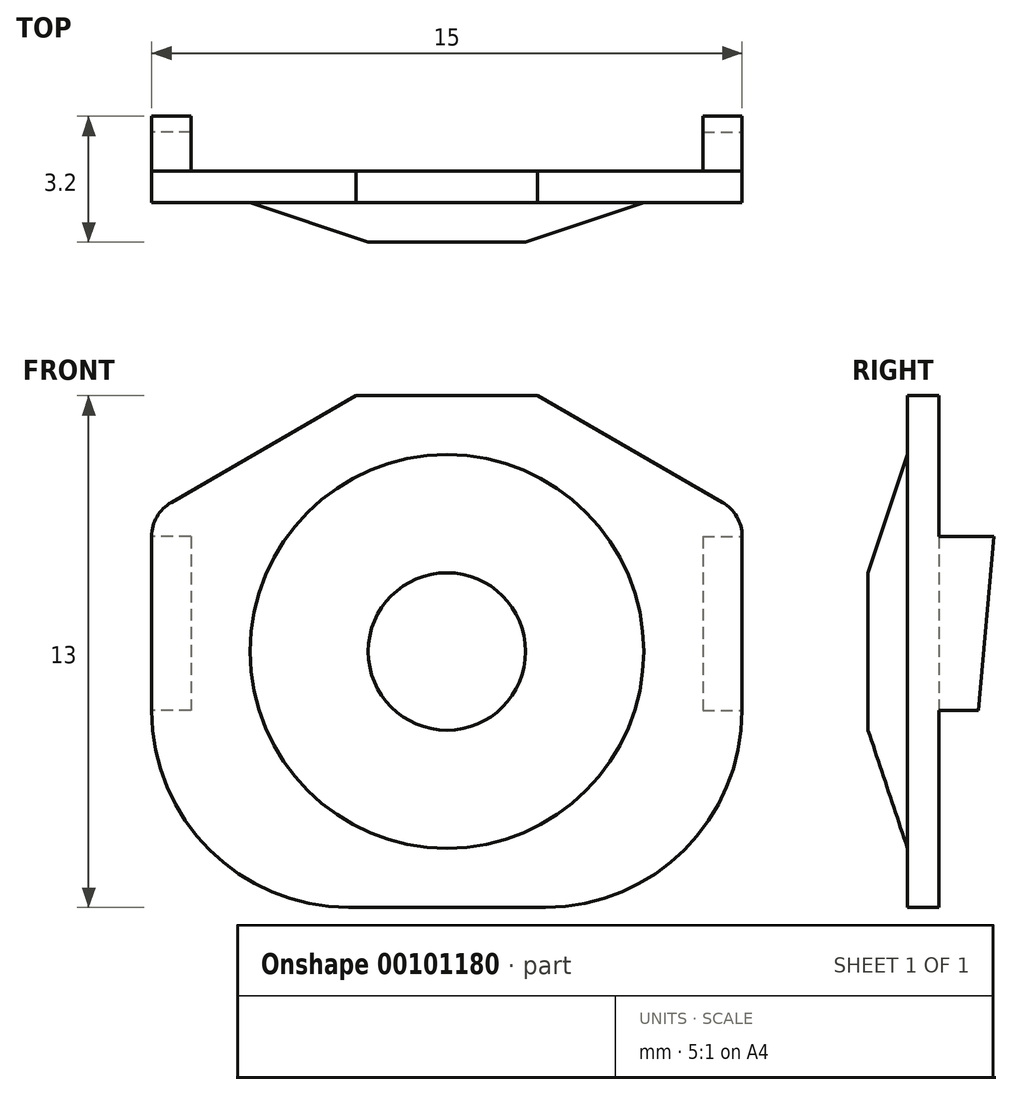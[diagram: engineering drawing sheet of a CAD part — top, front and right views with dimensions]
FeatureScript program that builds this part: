
annotation { "Feature Type Name" : "Feature", "Feature Type Description" : "" }
export const myFeature = defineFeature(function(context is Context, id is Id, definition is map)
    precondition{}
    {
        {
            var Q0;
            Q0=qCreatedBy(makeId("Front.planeOp"),FACE);
            var sketch = newSketch(context, id + "F0", { "sketchPlane" : qUnion([Q0])});
            skLineSegment(sketch, "E0.bottom", {"start": v(2.3, 6.5) * mm, "end": v(-2.3, 6.5) * mm});
            skLineSegment(sketch, "E0.top", {"start": v(7.5, -6.5) * mm, "end": v(-7.5, -6.5) * mm});
            skLineSegment(sketch, "E0.left", {"start": v(7.5, 3.5) * mm, "end": v(7.5, -6.5) * mm});
            skLineSegment(sketch, "E0.right", {"start": v(-7.5, 3.5) * mm, "end": v(-7.5, -6.5) * mm});
            skPoint(sketch, "E0.middle", {"position": v(0, 0) * mm});
            skLineSegment(sketch, "E1", {"start": v(-7.5, 3.5) * mm, "end": v(-2.3, 6.5) * mm});
            skLineSegment(sketch, "E2", {"start": v(2.3, 6.5) * mm, "end": v(7.5, 3.5) * mm});
            skPoint(sketch, "E3.orphan", {"position": v(-7.5, 6.5) * mm});
            skPoint(sketch, "E4.orphan", {"position": v(7.5, 6.5) * mm});
            skSolve(sketch);
        }
        {
            var Q0;
            Q0=makeQuery(id+"F0.imprint","IMPRINT",FACE,{"disambiguationData":[TD([[makeQuery(id+"F0.imprint","IMPRINT",EDGE,{"derivedFrom":sQuery(id+"F0.wireOp",EDGE,"E0.bottom")}),1.0]])]});
            extrude(context, id + "F1", {"entities" : qUnion([Q0]), "offsetDistance" : 25 * mm, "depth" : 0.8 * mm});
        }
        {
            var Q0;
            Q0=makeQuery(id+"F1.opExtrude","SWEPT_EDGE",EDGE,{"disambiguationData":[OSD([sQuery(id+"F0.wireOp",EDGE,"E0.top"),sQuery(id+"F0.wireOp",EDGE,"E0.left")])]});
            var Q1;
            Q1=makeQuery(id+"F1.opExtrude","SWEPT_EDGE",EDGE,{"disambiguationData":[OSD([sQuery(id+"F0.wireOp",EDGE,"E0.top"),sQuery(id+"F0.wireOp",EDGE,"E0.right")])]});
            fillet(context, id + "F2", {"entities" : qUnion([Q0, Q1]), "radius" : 5 * mm, "tangentPropagation" : true, "allowEdgeOverflow" : false});
        }
        {
            var Q0;
            Q0=makeQuery(id+"F1.opExtrude","SWEPT_EDGE",EDGE,{"disambiguationData":[OSD([sQuery(id+"F0.wireOp",EDGE,"E0.left"),sQuery(id+"F0.wireOp",EDGE,"E2")])]});
            var Q1;
            Q1=makeQuery(id+"F1.opExtrude","SWEPT_EDGE",EDGE,{"disambiguationData":[OSD([sQuery(id+"F0.wireOp",EDGE,"E0.right"),sQuery(id+"F0.wireOp",EDGE,"E1")])]});
            fillet(context, id + "F3", {"entities" : qUnion([Q0, Q1]), "radius" : 1 * mm, "tangentPropagation" : true, "allowEdgeOverflow" : false});
        }
        {
            var Q0;
            Q0=makeQuery(id+"F1.opExtrude","CAP_FACE",FACE,{"disambiguationData":[OSD([sQuery(id+"F0.wireOp",EDGE,"E0.bottom"),sQuery(id+"F0.wireOp",EDGE,"E0.top"),sQuery(id+"F0.wireOp",EDGE,"E0.left"),sQuery(id+"F0.wireOp",EDGE,"E0.right"),sQuery(id+"F0.wireOp",EDGE,"E1"),sQuery(id+"F0.wireOp",EDGE,"E2")])],"isStart":false});
            var sketch = newSketch(context, id + "F4", { "sketchPlane" : qUnion([Q0])});
            skCircle(sketch, "E5", {"center": v(0, 0) * mm, "radius": 5 * mm});
            skSolve(sketch);
        }
        {
            var Q0;
            Q0 = qSketchRegion(id + "F4", true);
            extrude(context, id + "F5", {"entities" : qUnion([Q0]), "operationType" : NewBodyOperationType.ADD, "depth" : 1 * mm});
        }
        {
            var Q0;
            Q0=makeQuery(id+"F5.opExtrude","CAP_EDGE",EDGE,{"disambiguationData":[OSD([sQuery(id+"F4.wireOp",EDGE,"E5")])],"isStart":false});
            chamfer(context, id + "F6", {"entities" : qUnion([Q0]), "chamferType" : ChamferType.TWO_OFFSETS, "width1" : 1 * mm, "oppositeDirection" : true, "width2" : 3 * mm, "tangentPropagation" : true});
        }
        {
            var Q0;
            Q0=makeQuery(id+"F1.opExtrude","SWEPT_FACE",FACE,{"disambiguationData":[OSD([sQuery(id+"F0.wireOp",EDGE,"E0.left")])]});
            var sketch = newSketch(context, id + "F7", { "sketchPlane" : qUnion([Q0])});
            skLineSegment(sketch, "E6", {"start": v(0, 2.92) * mm, "end": v(1.4, 2.92) * mm});
            skLineSegment(sketch, "E7", {"start": v(1.4, 2.92) * mm, "end": v(1, -1.5) * mm});
            skLineSegment(sketch, "E8", {"start": v(1, -1.5) * mm, "end": v(0, -1.5) * mm});
            skLineSegment(sketch, "E9", {"start": v(0, -1.5) * mm, "end": v(0, 2.92) * mm});
            skSolve(sketch);
        }
        {
            var Q0;
            Q0 = qSketchRegion(id + "F7", true);
            extrude(context, id + "F8", {"entities" : qUnion([Q0]), "operationType" : NewBodyOperationType.ADD, "oppositeDirection" : true, "depth" : 1 * mm});
        }
        {
            var Q0;
            Q0=makeQuery(id+"F1.opExtrude","SWEPT_BODY",BODY,{"disambiguationData":[OSD([sQuery(id+"F0.wireOp",EDGE,"E0.bottom"),sQuery(id+"F0.wireOp",EDGE,"E0.top"),sQuery(id+"F0.wireOp",EDGE,"E0.left"),sQuery(id+"F0.wireOp",EDGE,"E0.right"),sQuery(id+"F0.wireOp",EDGE,"E1"),sQuery(id+"F0.wireOp",EDGE,"E2")])]});
            var Q1;
            Q1=qCreatedBy(makeId("Right.planeOp"),FACE);
            mirror(context, id + "F9", {"operationType" : NewBodyOperationType.ADD, "entities" : qUnion([Q0]), "mirrorPlane" : qUnion([Q1])});
        }
    });
